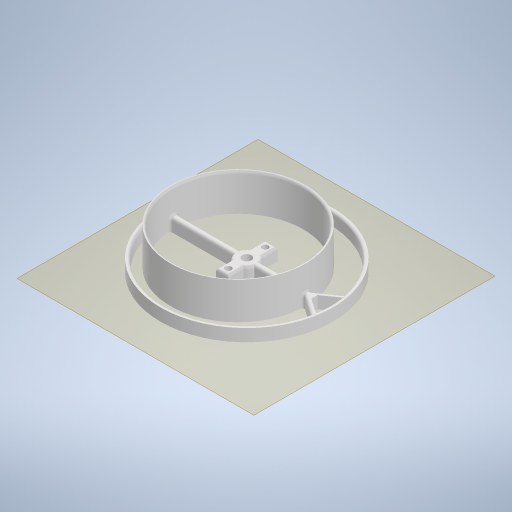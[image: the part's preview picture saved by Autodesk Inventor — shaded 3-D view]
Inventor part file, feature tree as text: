
AUTODESK INVENTOR PART (.ipt)
format: ipt  version: 2023.2 (Build 272271030, 271C)  size: 473,600 bytes
history: native  units: in
note: dims shown in document units (in); Inventor stores cm internally (conversion verified against a paired STEP export)
features: fillet x4, other x4, extrude x2, sketch x2, reference x2, plane x1
ambient origin geometry x8: Origin, YZ Plane, XZ Plane, XY Plane, X Axis, Y Axis, Z Axis, Center Point
bodies: Solid1 (feature_tree)
feature tree (15):
  extrude  "Extrusion1"  Depth=0.2894in
  fillet  "Fillet2"  Radius=0.1969in
  plane  "Work Plane1"
  extrude  "Extrusion2"  Depth=0.0591in
  fillet  "Fillet3"  Radius=0.3937in
  fillet  "Fillet4"  Radius=0.1181in
  fillet  "Fillet5"  Radius=0.1181in
  sketch  "Sketch1"  dims[d0=0.1969in d1=5.5118in d2=0.2894in d3=0.1969in]
  reference  "Reference1"
  reference  "Reference2"
  sketch  "Sketch2"  dims[d4=0.1969in d5=0.3543in d6=0.1181in d7=0.1181in d8=0.3937in d9=0.0in d12=0.1181in d14=0.1181in d15=0.1181in d16=2.1654in d17=0.1969in d18=0.3937in d19=0.3937in d20=0.4928in d21=1.9616in d22=0.0787in d23=4.3307in d24=0.2756in d25=0.0787in d26=1.1811in d27=0.0in d28=0.0787in d29=0.0787in d30=0.0591in]
  other  "Assembly1"
  other  "SkimmerLid:1"
  other  "<userpath>\Dropbox\elec\Mechanical\SkimmerSwabbie\_Design_SkimmerLid.iam"
  other  "_Design_SkimmerLid.iam"
